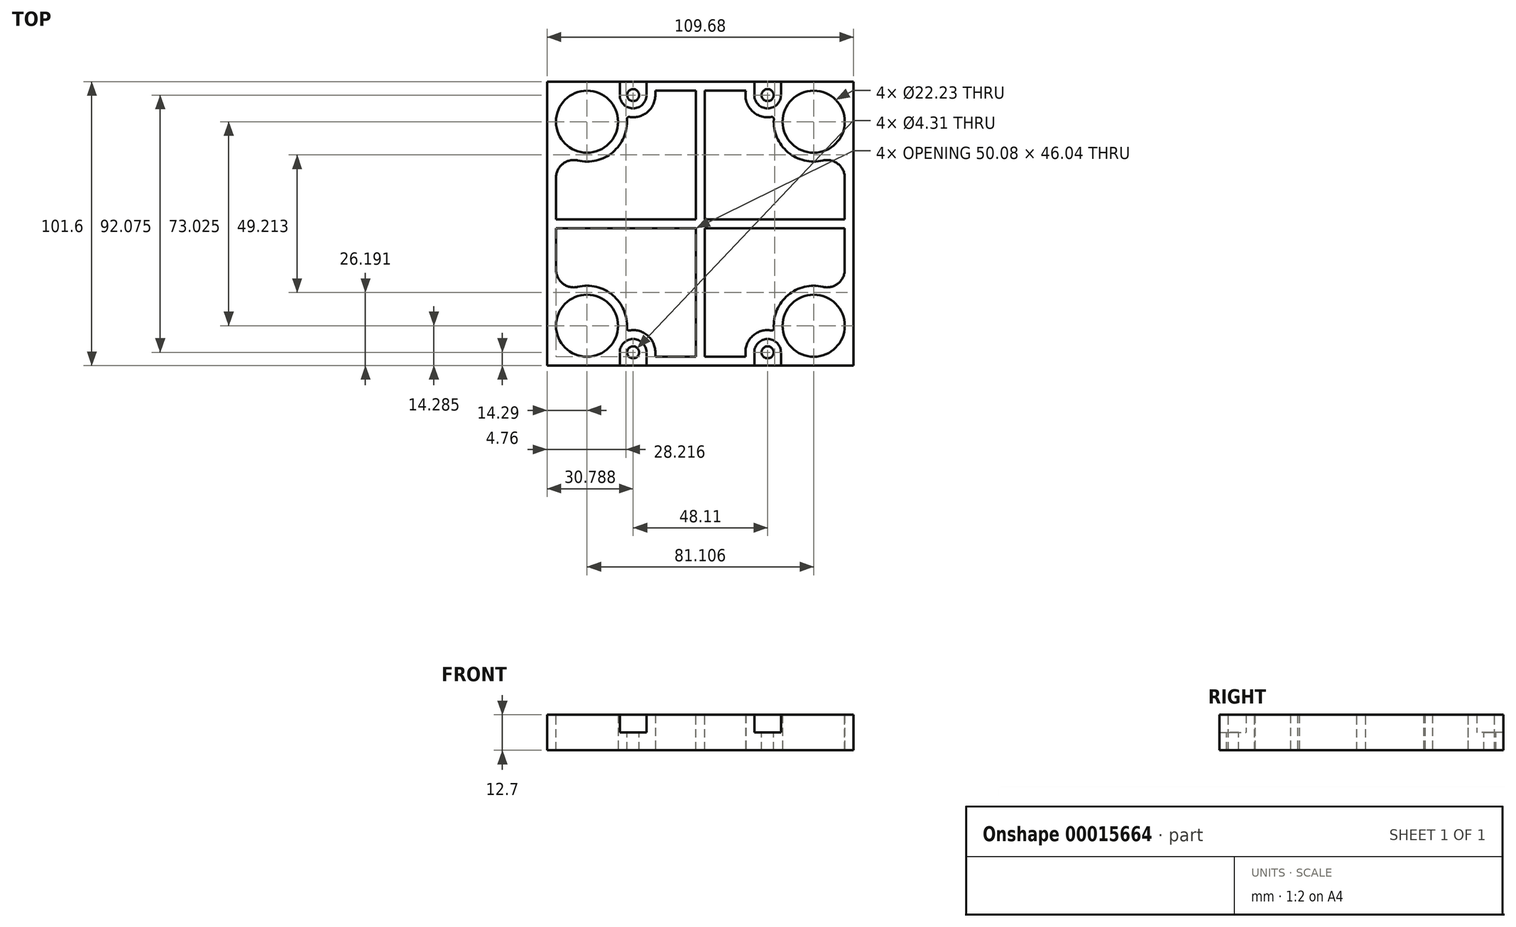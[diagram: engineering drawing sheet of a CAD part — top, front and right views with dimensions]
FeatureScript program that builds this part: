
annotation { "Feature Type Name" : "Feature", "Feature Type Description" : "" }
export const myFeature = defineFeature(function(context is Context, id is Id, definition is map)
    precondition{}
    {
        {
            var Q0;
            Q0=qCreatedBy(makeId("Top.planeOp"),FACE);
            var sketch = newSketch(context, id + "F0", { "sketchPlane" : qUnion([Q0])});
            skCircle(sketch, "E0", {"center": v(0, 0) * mm, "radius": 11.11 * mm});
            skLineSegment(sketch, "E1", {"start": v(0, 0) * mm, "end": v(81.1, 0) * mm, "construction": true});
            skLineSegment(sketch, "E2.left", {"start": v(-14.29, 14.29) * mm, "end": v(-14.29, -87.31) * mm});
            skLineSegment(sketch, "E2.right", {"start": v(95.4, 14.29) * mm, "end": v(95.4, -87.31) * mm});
            skPoint(sketch, "E2.middle", {"position": v(40.55, -36.51) * mm});
            skLineSegment(sketch, "E3", {"start": v(81.1, 0) * mm, "end": v(95.4, 0) * mm, "construction": true});
            skLineSegment(sketch, "E4", {"start": v(0, 0) * mm, "end": v(-14.29, 0) * mm, "construction": true});
            skCircle(sketch, "E5", {"center": v(81.1, 0) * mm, "radius": 11.11 * mm});
            skLineSegment(sketch, "E6", {"start": v(-14.29, 14.29) * mm, "end": v(11.74, 14.29) * mm});
            skLineSegment(sketch, "E7", {"start": v(95.4, 14.29) * mm, "end": v(69.37, 14.29) * mm});
            skLineSegment(sketch, "E8.bottom", {"start": v(11.74, 14.29) * mm, "end": v(21.26, 14.29) * mm, "construction": true});
            skLineSegment(sketch, "E8.top", {"start": v(11.74, 9.52) * mm, "end": v(21.26, 9.52) * mm, "construction": true});
            skLineSegment(sketch, "E8.left", {"start": v(11.74, 14.29) * mm, "end": v(11.74, 9.52) * mm});
            skLineSegment(sketch, "E8.right", {"start": v(21.26, 14.29) * mm, "end": v(21.26, 9.52) * mm});
            skLineSegment(sketch, "E9.bottom", {"start": v(69.37, 14.29) * mm, "end": v(59.85, 14.29) * mm, "construction": true});
            skLineSegment(sketch, "E9.top", {"start": v(69.37, 9.52) * mm, "end": v(59.85, 9.52) * mm, "construction": true});
            skLineSegment(sketch, "E9.left", {"start": v(69.37, 14.29) * mm, "end": v(69.37, 9.53) * mm});
            skLineSegment(sketch, "E9.right", {"start": v(59.85, 14.29) * mm, "end": v(59.85, 9.53) * mm});
            skCircle(sketch, "E10", {"center": v(16.5, 9.52) * mm, "radius": 7.94 * mm, "construction": true});
            skArc(sketch, "E11", {"start": v(21.26, 9.52) * mm, "mid": v(16.5, 14.29) * mm, "end": v(11.74, 9.52) * mm, "construction": true});
            skArc(sketch, "E12", {"start": v(11.74, 9.52) * mm, "mid": v(16.5, 4.76) * mm, "end": v(21.26, 9.52) * mm});
            skArc(sketch, "E13", {"start": v(59.85, 9.53) * mm, "mid": v(64.6, 4.76) * mm, "end": v(69.37, 9.53) * mm});
            skLineSegment(sketch, "E14", {"start": v(21.26, 14.29) * mm, "end": v(59.85, 14.29) * mm});
            skLineSegment(sketch, "E15", {"start": v(-14.29, -87.31) * mm, "end": v(11.74, -87.31) * mm});
            skLineSegment(sketch, "E16", {"start": v(95.4, -87.31) * mm, "end": v(69.37, -87.31) * mm});
            skLineSegment(sketch, "E17.bottom", {"start": v(11.74, -87.31) * mm, "end": v(21.26, -87.31) * mm, "construction": true});
            skLineSegment(sketch, "E17.top", {"start": v(11.74, -82.55) * mm, "end": v(21.26, -82.55) * mm, "construction": true});
            skLineSegment(sketch, "E17.left", {"start": v(11.74, -87.31) * mm, "end": v(11.74, -82.55) * mm});
            skLineSegment(sketch, "E17.right", {"start": v(21.26, -87.31) * mm, "end": v(21.26, -82.55) * mm});
            skLineSegment(sketch, "E18.bottom", {"start": v(69.37, -87.31) * mm, "end": v(59.85, -87.31) * mm, "construction": true});
            skLineSegment(sketch, "E18.top", {"start": v(69.37, -82.55) * mm, "end": v(59.85, -82.55) * mm, "construction": true});
            skLineSegment(sketch, "E18.left", {"start": v(69.37, -87.31) * mm, "end": v(69.37, -82.55) * mm});
            skLineSegment(sketch, "E18.right", {"start": v(59.85, -87.31) * mm, "end": v(59.85, -82.55) * mm});
            skLineSegment(sketch, "E19", {"start": v(21.26, -87.31) * mm, "end": v(59.85, -87.31) * mm});
            skArc(sketch, "E20", {"start": v(21.26, -82.55) * mm, "mid": v(16.5, -77.79) * mm, "end": v(11.74, -82.55) * mm});
            skArc(sketch, "E21", {"start": v(69.37, -82.55) * mm, "mid": v(64.6, -77.79) * mm, "end": v(59.85, -82.55) * mm});
            skLineSegment(sketch, "E22", {"start": v(40.55, 0) * mm, "end": v(40.55, 14.29) * mm, "construction": true});
            skLineSegment(sketch, "E23", {"start": v(-14.29, -73.03) * mm, "end": v(0, -73.03) * mm, "construction": true});
            skLineSegment(sketch, "E24", {"start": v(0, -73.03) * mm, "end": v(81.1, -73.03) * mm, "construction": true});
            skLineSegment(sketch, "E25", {"start": v(81.1, -73.03) * mm, "end": v(95.4, -73.03) * mm, "construction": true});
            skLineSegment(sketch, "E26", {"start": v(40.55, -73.03) * mm, "end": v(40.55, -87.31) * mm, "construction": true});
            skCircle(sketch, "E27", {"center": v(0, -73.02) * mm, "radius": 11.11 * mm});
            skCircle(sketch, "E28", {"center": v(81.1, -73.03) * mm, "radius": 11.11 * mm});
            skSolve(sketch);
        }
        {
            var Q0;
            Q0=qSketchRegion(id+"F0",true);
            extrude(context, id + "F1", {"entities" : qUnion([Q0]), "depth" : 6.35 * mm});
        }
        {
            var Q0;
            Q0=makeQuery(id+"F1.opExtrude","CAP_FACE",FACE,{"disambiguationData":[OSD([sQuery(id+"F0.wireOp",EDGE,"E0"),sQuery(id+"F0.wireOp",EDGE,"E2.left"),sQuery(id+"F0.wireOp",EDGE,"E2.right"),sQuery(id+"F0.wireOp",EDGE,"E5"),sQuery(id+"F0.wireOp",EDGE,"E6"),sQuery(id+"F0.wireOp",EDGE,"E7"),sQuery(id+"F0.wireOp",EDGE,"E8.left"),sQuery(id+"F0.wireOp",EDGE,"E8.right"),sQuery(id+"F0.wireOp",EDGE,"E9.left"),sQuery(id+"F0.wireOp",EDGE,"E9.right"),sQuery(id+"F0.wireOp",EDGE,"E12"),sQuery(id+"F0.wireOp",EDGE,"E13"),sQuery(id+"F0.wireOp",EDGE,"E14"),sQuery(id+"F0.wireOp",EDGE,"E15"),sQuery(id+"F0.wireOp",EDGE,"E16"),sQuery(id+"F0.wireOp",EDGE,"E17.left"),sQuery(id+"F0.wireOp",EDGE,"E17.right"),sQuery(id+"F0.wireOp",EDGE,"E18.left"),sQuery(id+"F0.wireOp",EDGE,"E18.right"),sQuery(id+"F0.wireOp",EDGE,"E19"),sQuery(id+"F0.wireOp",EDGE,"E20"),sQuery(id+"F0.wireOp",EDGE,"E21")])],"isStart":true});
            var sketch = newSketch(context, id + "F2", { "sketchPlane" : qUnion([Q0])});
            skLineSegment(sketch, "E29.bottom", {"start": v(11.74, -14.29) * mm, "end": v(69.37, -14.29) * mm});
            skLineSegment(sketch, "E29.top", {"start": v(11.74, 87.31) * mm, "end": v(69.37, 87.31) * mm});
            skLineSegment(sketch, "E29.left", {"start": v(11.74, -14.29) * mm, "end": v(11.74, 87.31) * mm, "construction": true});
            skLineSegment(sketch, "E29.right", {"start": v(69.37, -14.29) * mm, "end": v(69.37, 87.31) * mm, "construction": true});
            skCircle(sketch, "E30", {"center": v(16.5, 82.55) * mm, "radius": 2.15 * mm});
            skCircle(sketch, "E31", {"center": v(16.5, -9.52) * mm, "radius": 2.15 * mm});
            skCircle(sketch, "E32", {"center": v(64.6, 82.55) * mm, "radius": 2.15 * mm});
            skCircle(sketch, "E33", {"center": v(64.6, -9.53) * mm, "radius": 2.15 * mm});
            skSolve(sketch);
        }
        {
            var Q0;
            {var subQ19=sQuery(id+"F0.wireOp",EDGE,"E0");var subQ20=makeQuery(id+"F1.opExtrude","CAP_EDGE",EDGE,{"disambiguationData":[OSD([subQ19])],"isStart":true});Q0=makeQuery(id+"F2.imprint","IMPRINT",FACE,{"disambiguationData":[TD([[makeQuery(id+"F2.imprint","IMPRINT",EDGE,{"derivedFrom":subQ20}),1.0]])]});}
            var Q1;
            Q1=makeQuery(id+"F2.imprint","IMPRINT",FACE,{"disambiguationData":[TD([[makeQuery(id+"F2.imprint","IMPRINT",EDGE,{"derivedFrom":sQuery(id+"F2.wireOp",EDGE,"E31")}),-1.0]])]});
            var Q2;
            Q2=makeQuery(id+"F2.imprint","IMPRINT",FACE,{"disambiguationData":[TD([[makeQuery(id+"F2.imprint","IMPRINT",EDGE,{"derivedFrom":sQuery(id+"F2.wireOp",EDGE,"E33")}),-1.0]])]});
            var Q3;
            Q3=makeQuery(id+"F2.imprint","IMPRINT",FACE,{"disambiguationData":[TD([[makeQuery(id+"F2.imprint","IMPRINT",EDGE,{"derivedFrom":sQuery(id+"F2.wireOp",EDGE,"E32")}),-1.0]])]});
            var Q4;
            Q4=makeQuery(id+"F2.imprint","IMPRINT",FACE,{"disambiguationData":[TD([[makeQuery(id+"F2.imprint","IMPRINT",EDGE,{"derivedFrom":sQuery(id+"F2.wireOp",EDGE,"E30")}),-1.0]])]});
            extrude(context, id + "F3", {"entities" : qUnion([Q0, Q1, Q2, Q3, Q4]), "operationType" : NewBodyOperationType.ADD, "depth" : 6.35 * mm});
        }
        {
            var Q0;
            {var subQ0=sQuery(id+"F0.wireOp",EDGE,"E28");var subQ1=sQuery(id+"F0.wireOp",EDGE,"E27");var subQ2=sQuery(id+"F0.wireOp",EDGE,"E21");var subQ3=sQuery(id+"F0.wireOp",EDGE,"E20");var subQ4=sQuery(id+"F0.wireOp",EDGE,"E19");var subQ5=sQuery(id+"F0.wireOp",EDGE,"E18.right");var subQ6=sQuery(id+"F0.wireOp",EDGE,"E18.left");var subQ7=sQuery(id+"F0.wireOp",EDGE,"E17.right");var subQ8=sQuery(id+"F0.wireOp",EDGE,"E17.left");var subQ9=sQuery(id+"F0.wireOp",EDGE,"E16");var subQ10=sQuery(id+"F0.wireOp",EDGE,"E15");var subQ11=sQuery(id+"F0.wireOp",EDGE,"E14");var subQ12=sQuery(id+"F0.wireOp",EDGE,"E13");var subQ13=sQuery(id+"F0.wireOp",EDGE,"E12");var subQ14=sQuery(id+"F0.wireOp",EDGE,"E9.right");var subQ15=sQuery(id+"F0.wireOp",EDGE,"E9.left");var subQ16=sQuery(id+"F0.wireOp",EDGE,"E8.right");var subQ17=sQuery(id+"F0.wireOp",EDGE,"E8.left");var subQ18=sQuery(id+"F0.wireOp",EDGE,"E7");var subQ19=sQuery(id+"F0.wireOp",EDGE,"E6");var subQ20=sQuery(id+"F0.wireOp",EDGE,"E5");var subQ21=sQuery(id+"F0.wireOp",EDGE,"E2.right");var subQ22=sQuery(id+"F0.wireOp",EDGE,"E2.left");var subQ23=sQuery(id+"F0.wireOp",EDGE,"E0");Q0=makeQuery(id+"FTSSr8BHqQrdgFx_1.boolean.opBoolean","MERGE",FACE,{"derivedFrom":[makeQuery(id+"F1.opExtrude","CAP_FACE",FACE,{"disambiguationData":[OSD([subQ23,subQ22,subQ21,subQ20,subQ19,subQ18,subQ17,subQ16,subQ15,subQ14,subQ13,subQ12,subQ11,subQ10,subQ9,subQ8,subQ7,subQ6,subQ5,subQ4,subQ3,subQ2,subQ1,subQ0])],"isStart":false}),makeQuery(id+"FTSSr8BHqQrdgFx_1.opExtrude","CAP_FACE",FACE,{"disambiguationData":[OSD([subQ23,subQ22,subQ21,subQ20,subQ19,subQ18,subQ17,subQ16,subQ15,subQ14,subQ13,subQ12,subQ11,subQ10,subQ9,subQ8,subQ7,subQ6,subQ5,subQ4,subQ3,subQ2,subQ1,subQ0]),ownerDisambiguation([makeQuery(id+"FTSSr8BHqQrdgFx_1.opExtrude","SWEPT_BODY",BODY,{"disambiguationData":[OSD([subQ23,subQ22,subQ21,subQ20,subQ19,subQ18,subQ17,subQ16,subQ15,subQ14,subQ13,subQ12,subQ11,subQ10,subQ9,subQ8,subQ7,subQ6,subQ5,subQ4,subQ3,subQ2,subQ1,subQ0]),TDD([makeQuery(id+"Fb57pSd5HtlTtCQ_1.opShell","OFFSET_FACE",FACE,{"disambiguationData":[OSD([subQ23,subQ22,subQ21,subQ20,subQ19,subQ18,subQ17,subQ16,subQ15,subQ14,subQ13,subQ12,subQ11,subQ10,subQ9,subQ8,subQ7,subQ6,subQ5,subQ4,subQ3,subQ2,subQ1,subQ0]),OD(0.0)]})])]})])],"isStart":false}),makeQuery(id+"FTSSr8BHqQrdgFx_1.opExtrude","CAP_FACE",FACE,{"disambiguationData":[OSD([subQ23,subQ22,subQ21,subQ20,subQ19,subQ18,subQ17,subQ16,subQ15,subQ14,subQ13,subQ12,subQ11,subQ10,subQ9,subQ8,subQ7,subQ6,subQ5,subQ4,subQ3,subQ2,subQ1,subQ0]),ownerDisambiguation([makeQuery(id+"FTSSr8BHqQrdgFx_1.opExtrude","SWEPT_BODY",BODY,{"disambiguationData":[OSD([subQ23,subQ22,subQ21,subQ20,subQ19,subQ18,subQ17,subQ16,subQ15,subQ14,subQ13,subQ12,subQ11,subQ10,subQ9,subQ8,subQ7,subQ6,subQ5,subQ4,subQ3,subQ2,subQ1,subQ0]),TDD([makeQuery(id+"Fb57pSd5HtlTtCQ_1.opShell","OFFSET_FACE",FACE,{"disambiguationData":[OSD([subQ23,subQ22,subQ21,subQ20,subQ19,subQ18,subQ17,subQ16,subQ15,subQ14,subQ13,subQ12,subQ11,subQ10,subQ9,subQ8,subQ7,subQ6,subQ5,subQ4,subQ3,subQ2,subQ1,subQ0]),OD(1.0)]})])]})])],"isStart":false}),makeQuery(id+"FTSSr8BHqQrdgFx_1.opExtrude","CAP_FACE",FACE,{"disambiguationData":[OSD([subQ23,subQ22,subQ21,subQ20,subQ19,subQ18,subQ17,subQ16,subQ15,subQ14,subQ13,subQ12,subQ11,subQ10,subQ9,subQ8,subQ7,subQ6,subQ5,subQ4,subQ3,subQ2,subQ1,subQ0]),ownerDisambiguation([makeQuery(id+"FTSSr8BHqQrdgFx_1.opExtrude","SWEPT_BODY",BODY,{"disambiguationData":[OSD([subQ23,subQ22,subQ21,subQ20,subQ19,subQ18,subQ17,subQ16,subQ15,subQ14,subQ13,subQ12,subQ11,subQ10,subQ9,subQ8,subQ7,subQ6,subQ5,subQ4,subQ3,subQ2,subQ1,subQ0]),TDD([makeQuery(id+"Fb57pSd5HtlTtCQ_1.opShell","OFFSET_FACE",FACE,{"disambiguationData":[OSD([subQ23,subQ22,subQ21,subQ20,subQ19,subQ18,subQ17,subQ16,subQ15,subQ14,subQ13,subQ12,subQ11,subQ10,subQ9,subQ8,subQ7,subQ6,subQ5,subQ4,subQ3,subQ2,subQ1,subQ0]),OD(4.0)]})])]})])],"isStart":false}),makeQuery(id+"FTSSr8BHqQrdgFx_1.opExtrude","CAP_FACE",FACE,{"disambiguationData":[OSD([subQ23,subQ22,subQ21,subQ20,subQ19,subQ18,subQ17,subQ16,subQ15,subQ14,subQ13,subQ12,subQ11,subQ10,subQ9,subQ8,subQ7,subQ6,subQ5,subQ4,subQ3,subQ2,subQ1,subQ0]),ownerDisambiguation([makeQuery(id+"FTSSr8BHqQrdgFx_1.opExtrude","SWEPT_BODY",BODY,{"disambiguationData":[OSD([subQ23,subQ22,subQ21,subQ20,subQ19,subQ18,subQ17,subQ16,subQ15,subQ14,subQ13,subQ12,subQ11,subQ10,subQ9,subQ8,subQ7,subQ6,subQ5,subQ4,subQ3,subQ2,subQ1,subQ0]),TDD([makeQuery(id+"Fb57pSd5HtlTtCQ_1.opShell","OFFSET_FACE",FACE,{"disambiguationData":[OSD([subQ23,subQ22,subQ21,subQ20,subQ19,subQ18,subQ17,subQ16,subQ15,subQ14,subQ13,subQ12,subQ11,subQ10,subQ9,subQ8,subQ7,subQ6,subQ5,subQ4,subQ3,subQ2,subQ1,subQ0]),OD(3.0)]})])]})])],"isStart":false})]});}
            shell(context, id + "F4", {"entities" : qUnion([Q0]), "thickness" : 3.17 * mm});
        }
        {
            var Q0;
            Q0=makeQuery(id+"F4.opShell","OFFSET_FACE",FACE,{"disambiguationData":[OSD([sQuery(id+"F0.wireOp",EDGE,"E0"),sQuery(id+"F0.wireOp",EDGE,"E2.left"),sQuery(id+"F0.wireOp",EDGE,"E2.right"),sQuery(id+"F0.wireOp",EDGE,"E5"),sQuery(id+"F0.wireOp",EDGE,"E6"),sQuery(id+"F0.wireOp",EDGE,"E7"),sQuery(id+"F0.wireOp",EDGE,"E8.left"),sQuery(id+"F0.wireOp",EDGE,"E8.right"),sQuery(id+"F0.wireOp",EDGE,"E9.left"),sQuery(id+"F0.wireOp",EDGE,"E9.right"),sQuery(id+"F0.wireOp",EDGE,"E12"),sQuery(id+"F0.wireOp",EDGE,"E13"),sQuery(id+"F0.wireOp",EDGE,"E14"),sQuery(id+"F0.wireOp",EDGE,"E15"),sQuery(id+"F0.wireOp",EDGE,"E16"),sQuery(id+"F0.wireOp",EDGE,"E17.left"),sQuery(id+"F0.wireOp",EDGE,"E17.right"),sQuery(id+"F0.wireOp",EDGE,"E18.left"),sQuery(id+"F0.wireOp",EDGE,"E18.right"),sQuery(id+"F0.wireOp",EDGE,"E19"),sQuery(id+"F0.wireOp",EDGE,"E20"),sQuery(id+"F0.wireOp",EDGE,"E21"),sQuery(id+"F0.wireOp",EDGE,"E27"),sQuery(id+"F0.wireOp",EDGE,"E28"),sQuery(id+"F2.wireOp",EDGE,"E29.bottom"),sQuery(id+"F2.wireOp",EDGE,"E29.top"),sQuery(id+"F2.wireOp",EDGE,"E30"),sQuery(id+"F2.wireOp",EDGE,"E31"),sQuery(id+"F2.wireOp",EDGE,"E32"),sQuery(id+"F2.wireOp",EDGE,"E33")]),OD(0.0)]});
            var Q1;
            Q1=makeQuery(id+"F3.opExtrude","CAP_FACE",FACE,{"disambiguationData":[OSD([sQuery(id+"F0.wireOp",EDGE,"E0"),sQuery(id+"F0.wireOp",EDGE,"E2.left"),sQuery(id+"F0.wireOp",EDGE,"E2.right"),sQuery(id+"F0.wireOp",EDGE,"E5"),sQuery(id+"F0.wireOp",EDGE,"E6"),sQuery(id+"F0.wireOp",EDGE,"E7"),sQuery(id+"F0.wireOp",EDGE,"E8.left"),sQuery(id+"F0.wireOp",EDGE,"E8.right"),sQuery(id+"F0.wireOp",EDGE,"E9.left"),sQuery(id+"F0.wireOp",EDGE,"E9.right"),sQuery(id+"F0.wireOp",EDGE,"E12"),sQuery(id+"F0.wireOp",EDGE,"E13"),sQuery(id+"F0.wireOp",EDGE,"E14"),sQuery(id+"F0.wireOp",EDGE,"E15"),sQuery(id+"F0.wireOp",EDGE,"E16"),sQuery(id+"F0.wireOp",EDGE,"E17.left"),sQuery(id+"F0.wireOp",EDGE,"E17.right"),sQuery(id+"F0.wireOp",EDGE,"E18.left"),sQuery(id+"F0.wireOp",EDGE,"E18.right"),sQuery(id+"F0.wireOp",EDGE,"E19"),sQuery(id+"F0.wireOp",EDGE,"E20"),sQuery(id+"F0.wireOp",EDGE,"E21"),sQuery(id+"F0.wireOp",EDGE,"E27"),sQuery(id+"F0.wireOp",EDGE,"E28"),sQuery(id+"F2.wireOp",EDGE,"E29.bottom"),sQuery(id+"F2.wireOp",EDGE,"E29.top"),sQuery(id+"F2.wireOp",EDGE,"E30"),sQuery(id+"F2.wireOp",EDGE,"E31"),sQuery(id+"F2.wireOp",EDGE,"E32"),sQuery(id+"F2.wireOp",EDGE,"E33")])],"isStart":false});
            extrude(context, id + "F5", {"entities" : qUnion([Q0]), "operationType" : NewBodyOperationType.REMOVE, "endBound" : BoundingType.UP_TO_SURFACE, "oppositeDirection" : true, "endBoundEntityFace" : qUnion([Q1]), "depth" : 25.4 * mm});
        }
        {
            var Q0;
            Q0=makeQuery(id+"F4.opShell","OFFSET_FACE",FACE,{"disambiguationData":[OSD([sQuery(id+"F0.wireOp",EDGE,"E0"),sQuery(id+"F0.wireOp",EDGE,"E2.left"),sQuery(id+"F0.wireOp",EDGE,"E2.right"),sQuery(id+"F0.wireOp",EDGE,"E5"),sQuery(id+"F0.wireOp",EDGE,"E6"),sQuery(id+"F0.wireOp",EDGE,"E7"),sQuery(id+"F0.wireOp",EDGE,"E8.left"),sQuery(id+"F0.wireOp",EDGE,"E8.right"),sQuery(id+"F0.wireOp",EDGE,"E9.left"),sQuery(id+"F0.wireOp",EDGE,"E9.right"),sQuery(id+"F0.wireOp",EDGE,"E12"),sQuery(id+"F0.wireOp",EDGE,"E13"),sQuery(id+"F0.wireOp",EDGE,"E14"),sQuery(id+"F0.wireOp",EDGE,"E15"),sQuery(id+"F0.wireOp",EDGE,"E16"),sQuery(id+"F0.wireOp",EDGE,"E17.left"),sQuery(id+"F0.wireOp",EDGE,"E17.right"),sQuery(id+"F0.wireOp",EDGE,"E18.left"),sQuery(id+"F0.wireOp",EDGE,"E18.right"),sQuery(id+"F0.wireOp",EDGE,"E19"),sQuery(id+"F0.wireOp",EDGE,"E20"),sQuery(id+"F0.wireOp",EDGE,"E21"),sQuery(id+"F0.wireOp",EDGE,"E27"),sQuery(id+"F0.wireOp",EDGE,"E28"),sQuery(id+"F2.wireOp",EDGE,"E29.bottom"),sQuery(id+"F2.wireOp",EDGE,"E29.top"),sQuery(id+"F2.wireOp",EDGE,"E30"),sQuery(id+"F2.wireOp",EDGE,"E31"),sQuery(id+"F2.wireOp",EDGE,"E32"),sQuery(id+"F2.wireOp",EDGE,"E33")]),OD(1.0)]});
            var Q1;
            Q1=makeQuery(id+"F4.opShell","OFFSET_FACE",FACE,{"disambiguationData":[OSD([sQuery(id+"F0.wireOp",EDGE,"E0"),sQuery(id+"F0.wireOp",EDGE,"E2.left"),sQuery(id+"F0.wireOp",EDGE,"E2.right"),sQuery(id+"F0.wireOp",EDGE,"E5"),sQuery(id+"F0.wireOp",EDGE,"E6"),sQuery(id+"F0.wireOp",EDGE,"E7"),sQuery(id+"F0.wireOp",EDGE,"E15"),sQuery(id+"F0.wireOp",EDGE,"E16"),sQuery(id+"F0.wireOp",EDGE,"E27"),sQuery(id+"F0.wireOp",EDGE,"E28"),sQuery(id+"F2.wireOp",EDGE,"E29.bottom"),sQuery(id+"F2.wireOp",EDGE,"E29.top"),sQuery(id+"F2.wireOp",EDGE,"E30"),sQuery(id+"F2.wireOp",EDGE,"E31"),sQuery(id+"F2.wireOp",EDGE,"E32"),sQuery(id+"F2.wireOp",EDGE,"E33")]),OD(3.0)]});
            var Q2;
            Q2=makeQuery(id+"F4.opShell","OFFSET_FACE",FACE,{"disambiguationData":[OSD([sQuery(id+"F0.wireOp",EDGE,"E0"),sQuery(id+"F0.wireOp",EDGE,"E2.left"),sQuery(id+"F0.wireOp",EDGE,"E2.right"),sQuery(id+"F0.wireOp",EDGE,"E5"),sQuery(id+"F0.wireOp",EDGE,"E6"),sQuery(id+"F0.wireOp",EDGE,"E7"),sQuery(id+"F0.wireOp",EDGE,"E15"),sQuery(id+"F0.wireOp",EDGE,"E16"),sQuery(id+"F0.wireOp",EDGE,"E27"),sQuery(id+"F0.wireOp",EDGE,"E28"),sQuery(id+"F2.wireOp",EDGE,"E29.bottom"),sQuery(id+"F2.wireOp",EDGE,"E29.top"),sQuery(id+"F2.wireOp",EDGE,"E30"),sQuery(id+"F2.wireOp",EDGE,"E31"),sQuery(id+"F2.wireOp",EDGE,"E32"),sQuery(id+"F2.wireOp",EDGE,"E33")]),OD(4.0)]});
            var Q3;
            Q3=makeQuery(id+"F4.opShell","OFFSET_FACE",FACE,{"disambiguationData":[OSD([sQuery(id+"F0.wireOp",EDGE,"E0"),sQuery(id+"F0.wireOp",EDGE,"E2.left"),sQuery(id+"F0.wireOp",EDGE,"E2.right"),sQuery(id+"F0.wireOp",EDGE,"E5"),sQuery(id+"F0.wireOp",EDGE,"E6"),sQuery(id+"F0.wireOp",EDGE,"E7"),sQuery(id+"F0.wireOp",EDGE,"E15"),sQuery(id+"F0.wireOp",EDGE,"E16"),sQuery(id+"F0.wireOp",EDGE,"E27"),sQuery(id+"F0.wireOp",EDGE,"E28"),sQuery(id+"F2.wireOp",EDGE,"E29.bottom"),sQuery(id+"F2.wireOp",EDGE,"E29.top"),sQuery(id+"F2.wireOp",EDGE,"E30"),sQuery(id+"F2.wireOp",EDGE,"E31"),sQuery(id+"F2.wireOp",EDGE,"E32"),sQuery(id+"F2.wireOp",EDGE,"E33")]),OD(2.0)]});
            var Q4;
            Q4=makeQuery(id+"F1.opExtrude","CAP_FACE",FACE,{"disambiguationData":[OSD([sQuery(id+"F0.wireOp",EDGE,"E0"),sQuery(id+"F0.wireOp",EDGE,"E2.left"),sQuery(id+"F0.wireOp",EDGE,"E2.right"),sQuery(id+"F0.wireOp",EDGE,"E5"),sQuery(id+"F0.wireOp",EDGE,"E6"),sQuery(id+"F0.wireOp",EDGE,"E7"),sQuery(id+"F0.wireOp",EDGE,"E8.left"),sQuery(id+"F0.wireOp",EDGE,"E8.right"),sQuery(id+"F0.wireOp",EDGE,"E9.left"),sQuery(id+"F0.wireOp",EDGE,"E9.right"),sQuery(id+"F0.wireOp",EDGE,"E12"),sQuery(id+"F0.wireOp",EDGE,"E13"),sQuery(id+"F0.wireOp",EDGE,"E14"),sQuery(id+"F0.wireOp",EDGE,"E15"),sQuery(id+"F0.wireOp",EDGE,"E16"),sQuery(id+"F0.wireOp",EDGE,"E17.left"),sQuery(id+"F0.wireOp",EDGE,"E17.right"),sQuery(id+"F0.wireOp",EDGE,"E18.left"),sQuery(id+"F0.wireOp",EDGE,"E18.right"),sQuery(id+"F0.wireOp",EDGE,"E19"),sQuery(id+"F0.wireOp",EDGE,"E20"),sQuery(id+"F0.wireOp",EDGE,"E21"),sQuery(id+"F0.wireOp",EDGE,"E27"),sQuery(id+"F0.wireOp",EDGE,"E28")])],"isStart":false});
            extrude(context, id + "F6", {"entities" : qUnion([Q0, Q1, Q2, Q3]), "operationType" : NewBodyOperationType.ADD, "endBound" : BoundingType.UP_TO_SURFACE, "endBoundEntityFace" : qUnion([Q4]), "depth" : 25.4 * mm});
        }
        {
            var Q0;
            {var subQ0=sQuery(id+"F0.wireOp",EDGE,"E27");var subQ1=makeQuery(id+"F3.boolean.opBoolean","MERGE",FACE,{"derivedFrom":[makeQuery(id+"F1.opExtrude","SWEPT_FACE",FACE,{"disambiguationData":[OSD([subQ0])]}),makeQuery(id+"F3.opExtrude","SWEPT_FACE",FACE,{"disambiguationData":[OSD([subQ0])]})]});var subQ2=sQuery(id+"F0.wireOp",EDGE,"E2.left");var subQ3=makeQuery(id+"F3.boolean.opBoolean","MERGE",FACE,{"derivedFrom":[makeQuery(id+"F1.opExtrude","SWEPT_FACE",FACE,{"disambiguationData":[OSD([subQ2])]}),makeQuery(id+"F3.opExtrude","SWEPT_FACE",FACE,{"disambiguationData":[OSD([subQ2])]})]});var subQ4=sQuery(id+"F2.wireOp",EDGE,"E33");var subQ5=sQuery(id+"F2.wireOp",EDGE,"E32");var subQ6=sQuery(id+"F2.wireOp",EDGE,"E31");var subQ7=sQuery(id+"F2.wireOp",EDGE,"E30");var subQ8=sQuery(id+"F2.wireOp",EDGE,"E29.top");var subQ9=sQuery(id+"F2.wireOp",EDGE,"E29.bottom");var subQ10=sQuery(id+"F0.wireOp",EDGE,"E28");var subQ11=sQuery(id+"F0.wireOp",EDGE,"E16");var subQ12=sQuery(id+"F0.wireOp",EDGE,"E15");var subQ13=sQuery(id+"F0.wireOp",EDGE,"E7");var subQ14=sQuery(id+"F0.wireOp",EDGE,"E6");var subQ15=sQuery(id+"F0.wireOp",EDGE,"E5");var subQ16=sQuery(id+"F0.wireOp",EDGE,"E2.right");var subQ17=sQuery(id+"F0.wireOp",EDGE,"E0");Q0=makeQuery(id+"F5.boolean.opBoolean","MERGE",EDGE,{"derivedFrom":[makeQuery(id+"F4.opShell","TWEAK_EDGE",EDGE,{"disambiguationData":[OD(1.0)],"derivedFrom":[subQ3,subQ1]}),makeQuery(id+"F5.opExtrude","SWEPT_EDGE",EDGE,{"disambiguationData":[OSD([subQ17,subQ2,subQ16,subQ15,subQ14,subQ13,subQ12,subQ11,subQ0,subQ10,subQ9,subQ8,subQ7,subQ6,subQ5,subQ4]),TDD([makeQuery(id+"F4.opShell","TWEAK_VERTEX",VERTEX,{"disambiguationData":[OD(0.0)],"derivedFrom":[makeQuery(id+"F3.opExtrude","CAP_FACE",FACE,{"disambiguationData":[OSD([subQ17,subQ2,subQ16,subQ15,subQ14,subQ13,subQ12,subQ11,subQ0,subQ10,subQ9,subQ8,subQ7,subQ6,subQ5,subQ4])],"isStart":false}),subQ3,subQ1]})])]})]});}
            var Q1;
            {var subQ0=sQuery(id+"F0.wireOp",EDGE,"E2.left");var subQ1=makeQuery(id+"F3.boolean.opBoolean","MERGE",FACE,{"derivedFrom":[makeQuery(id+"F1.opExtrude","SWEPT_FACE",FACE,{"disambiguationData":[OSD([subQ0])]}),makeQuery(id+"F3.opExtrude","SWEPT_FACE",FACE,{"disambiguationData":[OSD([subQ0])]})]});var subQ2=sQuery(id+"F0.wireOp",EDGE,"E0");var subQ3=makeQuery(id+"F3.boolean.opBoolean","MERGE",FACE,{"derivedFrom":[makeQuery(id+"F1.opExtrude","SWEPT_FACE",FACE,{"disambiguationData":[OSD([subQ2])]}),makeQuery(id+"F3.opExtrude","SWEPT_FACE",FACE,{"disambiguationData":[OSD([subQ2])]})]});var subQ4=sQuery(id+"F2.wireOp",EDGE,"E33");var subQ5=sQuery(id+"F2.wireOp",EDGE,"E32");var subQ6=sQuery(id+"F2.wireOp",EDGE,"E31");var subQ7=sQuery(id+"F2.wireOp",EDGE,"E30");var subQ8=sQuery(id+"F2.wireOp",EDGE,"E29.top");var subQ9=sQuery(id+"F2.wireOp",EDGE,"E29.bottom");var subQ10=sQuery(id+"F0.wireOp",EDGE,"E28");var subQ11=sQuery(id+"F0.wireOp",EDGE,"E27");var subQ12=sQuery(id+"F0.wireOp",EDGE,"E16");var subQ13=sQuery(id+"F0.wireOp",EDGE,"E15");var subQ14=sQuery(id+"F0.wireOp",EDGE,"E7");var subQ15=sQuery(id+"F0.wireOp",EDGE,"E6");var subQ16=sQuery(id+"F0.wireOp",EDGE,"E5");var subQ17=sQuery(id+"F0.wireOp",EDGE,"E2.right");Q1=makeQuery(id+"F5.boolean.opBoolean","MERGE",EDGE,{"derivedFrom":[makeQuery(id+"F4.opShell","TWEAK_EDGE",EDGE,{"disambiguationData":[OD(0.0)],"derivedFrom":[subQ3,subQ1]}),makeQuery(id+"F5.opExtrude","SWEPT_EDGE",EDGE,{"disambiguationData":[OSD([subQ2,subQ0,subQ17,subQ16,subQ15,subQ14,subQ13,subQ12,subQ11,subQ10,subQ9,subQ8,subQ7,subQ6,subQ5,subQ4]),TDD([makeQuery(id+"F4.opShell","TWEAK_VERTEX",VERTEX,{"disambiguationData":[OD(0.0)],"derivedFrom":[makeQuery(id+"F3.opExtrude","CAP_FACE",FACE,{"disambiguationData":[OSD([subQ2,subQ0,subQ17,subQ16,subQ15,subQ14,subQ13,subQ12,subQ11,subQ10,subQ9,subQ8,subQ7,subQ6,subQ5,subQ4])],"isStart":false}),subQ3,subQ1]})])]})]});}
            var Q2;
            {var subQ0=sQuery(id+"F0.wireOp",EDGE,"E5");var subQ1=makeQuery(id+"F3.boolean.opBoolean","MERGE",FACE,{"derivedFrom":[makeQuery(id+"F1.opExtrude","SWEPT_FACE",FACE,{"disambiguationData":[OSD([subQ0])]}),makeQuery(id+"F3.opExtrude","SWEPT_FACE",FACE,{"disambiguationData":[OSD([subQ0])]})]});var subQ2=sQuery(id+"F0.wireOp",EDGE,"E2.right");var subQ3=makeQuery(id+"F3.boolean.opBoolean","MERGE",FACE,{"derivedFrom":[makeQuery(id+"F1.opExtrude","SWEPT_FACE",FACE,{"disambiguationData":[OSD([subQ2])]}),makeQuery(id+"F3.opExtrude","SWEPT_FACE",FACE,{"disambiguationData":[OSD([subQ2])]})]});var subQ4=sQuery(id+"F2.wireOp",EDGE,"E33");var subQ5=sQuery(id+"F2.wireOp",EDGE,"E32");var subQ6=sQuery(id+"F2.wireOp",EDGE,"E31");var subQ7=sQuery(id+"F2.wireOp",EDGE,"E30");var subQ8=sQuery(id+"F2.wireOp",EDGE,"E29.top");var subQ9=sQuery(id+"F2.wireOp",EDGE,"E29.bottom");var subQ10=sQuery(id+"F0.wireOp",EDGE,"E28");var subQ11=sQuery(id+"F0.wireOp",EDGE,"E27");var subQ12=sQuery(id+"F0.wireOp",EDGE,"E16");var subQ13=sQuery(id+"F0.wireOp",EDGE,"E15");var subQ14=sQuery(id+"F0.wireOp",EDGE,"E7");var subQ15=sQuery(id+"F0.wireOp",EDGE,"E6");var subQ16=sQuery(id+"F0.wireOp",EDGE,"E2.left");var subQ17=sQuery(id+"F0.wireOp",EDGE,"E0");Q2=makeQuery(id+"F5.boolean.opBoolean","MERGE",EDGE,{"derivedFrom":[makeQuery(id+"F4.opShell","TWEAK_EDGE",EDGE,{"disambiguationData":[OD(1.0)],"derivedFrom":[subQ3,subQ1]}),makeQuery(id+"F5.opExtrude","SWEPT_EDGE",EDGE,{"disambiguationData":[OSD([subQ17,subQ16,subQ2,subQ0,subQ15,subQ14,subQ13,subQ12,subQ11,subQ10,subQ9,subQ8,subQ7,subQ6,subQ5,subQ4]),TDD([makeQuery(id+"F4.opShell","TWEAK_VERTEX",VERTEX,{"disambiguationData":[OD(0.0)],"derivedFrom":[makeQuery(id+"F3.opExtrude","CAP_FACE",FACE,{"disambiguationData":[OSD([subQ17,subQ16,subQ2,subQ0,subQ15,subQ14,subQ13,subQ12,subQ11,subQ10,subQ9,subQ8,subQ7,subQ6,subQ5,subQ4])],"isStart":false}),subQ3,subQ1]})])]})]});}
            var Q3;
            {var subQ0=sQuery(id+"F0.wireOp",EDGE,"E28");var subQ1=makeQuery(id+"F3.boolean.opBoolean","MERGE",FACE,{"derivedFrom":[makeQuery(id+"F1.opExtrude","SWEPT_FACE",FACE,{"disambiguationData":[OSD([subQ0])]}),makeQuery(id+"F3.opExtrude","SWEPT_FACE",FACE,{"disambiguationData":[OSD([subQ0])]})]});var subQ2=sQuery(id+"F0.wireOp",EDGE,"E2.right");var subQ3=makeQuery(id+"F3.boolean.opBoolean","MERGE",FACE,{"derivedFrom":[makeQuery(id+"F1.opExtrude","SWEPT_FACE",FACE,{"disambiguationData":[OSD([subQ2])]}),makeQuery(id+"F3.opExtrude","SWEPT_FACE",FACE,{"disambiguationData":[OSD([subQ2])]})]});var subQ4=sQuery(id+"F2.wireOp",EDGE,"E33");var subQ5=sQuery(id+"F2.wireOp",EDGE,"E32");var subQ6=sQuery(id+"F2.wireOp",EDGE,"E31");var subQ7=sQuery(id+"F2.wireOp",EDGE,"E30");var subQ8=sQuery(id+"F2.wireOp",EDGE,"E29.top");var subQ9=sQuery(id+"F2.wireOp",EDGE,"E29.bottom");var subQ10=sQuery(id+"F0.wireOp",EDGE,"E27");var subQ11=sQuery(id+"F0.wireOp",EDGE,"E16");var subQ12=sQuery(id+"F0.wireOp",EDGE,"E15");var subQ13=sQuery(id+"F0.wireOp",EDGE,"E7");var subQ14=sQuery(id+"F0.wireOp",EDGE,"E6");var subQ15=sQuery(id+"F0.wireOp",EDGE,"E5");var subQ16=sQuery(id+"F0.wireOp",EDGE,"E2.left");var subQ17=sQuery(id+"F0.wireOp",EDGE,"E0");Q3=makeQuery(id+"F5.boolean.opBoolean","MERGE",EDGE,{"derivedFrom":[makeQuery(id+"F4.opShell","TWEAK_EDGE",EDGE,{"disambiguationData":[OD(1.0)],"derivedFrom":[subQ3,subQ1]}),makeQuery(id+"F5.opExtrude","SWEPT_EDGE",EDGE,{"disambiguationData":[OSD([subQ17,subQ16,subQ2,subQ15,subQ14,subQ13,subQ12,subQ11,subQ10,subQ0,subQ9,subQ8,subQ7,subQ6,subQ5,subQ4]),TDD([makeQuery(id+"F4.opShell","TWEAK_VERTEX",VERTEX,{"disambiguationData":[OD(0.0)],"derivedFrom":[makeQuery(id+"F3.opExtrude","CAP_FACE",FACE,{"disambiguationData":[OSD([subQ17,subQ16,subQ2,subQ15,subQ14,subQ13,subQ12,subQ11,subQ10,subQ0,subQ9,subQ8,subQ7,subQ6,subQ5,subQ4])],"isStart":false}),subQ3,subQ1]})])]})]});}
            fillet(context, id + "F7", {"entities" : qUnion([Q0, Q1, Q2, Q3]), "radius" : 6.35 * mm, "tangentPropagation" : true, "allowEdgeOverflow" : false});
        }
        {
            var Q0;
            {var subQ0=sQuery(id+"F0.wireOp",EDGE,"E27");var subQ1=sQuery(id+"F0.wireOp",EDGE,"E20");Q0=makeQuery(id+"F5.boolean.opBoolean","MERGE",EDGE,{"derivedFrom":[makeQuery(id+"F4.opShell","TWEAK_EDGE",EDGE,{"derivedFrom":[makeQuery(id+"F1.opExtrude","SWEPT_FACE",FACE,{"disambiguationData":[OSD([subQ1])]}),makeQuery(id+"F3.boolean.opBoolean","MERGE",FACE,{"derivedFrom":[makeQuery(id+"F1.opExtrude","SWEPT_FACE",FACE,{"disambiguationData":[OSD([subQ0])]}),makeQuery(id+"F3.opExtrude","SWEPT_FACE",FACE,{"disambiguationData":[OSD([subQ0])]})]})]}),makeQuery(id+"F5.opExtrude","SWEPT_EDGE",EDGE,{"disambiguationData":[OSD([sQuery(id+"F0.wireOp",EDGE,"E0"),sQuery(id+"F0.wireOp",EDGE,"E2.left"),sQuery(id+"F0.wireOp",EDGE,"E2.right"),sQuery(id+"F0.wireOp",EDGE,"E5"),sQuery(id+"F0.wireOp",EDGE,"E6"),sQuery(id+"F0.wireOp",EDGE,"E7"),sQuery(id+"F0.wireOp",EDGE,"E15"),sQuery(id+"F0.wireOp",EDGE,"E16"),subQ1,subQ0,sQuery(id+"F0.wireOp",EDGE,"E28"),sQuery(id+"F2.wireOp",EDGE,"E29.bottom"),sQuery(id+"F2.wireOp",EDGE,"E29.top"),sQuery(id+"F2.wireOp",EDGE,"E30"),sQuery(id+"F2.wireOp",EDGE,"E31"),sQuery(id+"F2.wireOp",EDGE,"E32"),sQuery(id+"F2.wireOp",EDGE,"E33")])]})]});}
            var Q1;
            {var subQ0=sQuery(id+"F0.wireOp",EDGE,"E12");var subQ1=sQuery(id+"F0.wireOp",EDGE,"E0");Q1=makeQuery(id+"F5.boolean.opBoolean","MERGE",EDGE,{"derivedFrom":[makeQuery(id+"F4.opShell","TWEAK_EDGE",EDGE,{"derivedFrom":[makeQuery(id+"F1.opExtrude","SWEPT_FACE",FACE,{"disambiguationData":[OSD([subQ0])]}),makeQuery(id+"F3.boolean.opBoolean","MERGE",FACE,{"derivedFrom":[makeQuery(id+"F1.opExtrude","SWEPT_FACE",FACE,{"disambiguationData":[OSD([subQ1])]}),makeQuery(id+"F3.opExtrude","SWEPT_FACE",FACE,{"disambiguationData":[OSD([subQ1])]})]})]}),makeQuery(id+"F5.opExtrude","SWEPT_EDGE",EDGE,{"disambiguationData":[OSD([subQ1,sQuery(id+"F0.wireOp",EDGE,"E2.left"),sQuery(id+"F0.wireOp",EDGE,"E2.right"),sQuery(id+"F0.wireOp",EDGE,"E5"),sQuery(id+"F0.wireOp",EDGE,"E6"),sQuery(id+"F0.wireOp",EDGE,"E7"),subQ0,sQuery(id+"F0.wireOp",EDGE,"E15"),sQuery(id+"F0.wireOp",EDGE,"E16"),sQuery(id+"F0.wireOp",EDGE,"E27"),sQuery(id+"F0.wireOp",EDGE,"E28"),sQuery(id+"F2.wireOp",EDGE,"E29.bottom"),sQuery(id+"F2.wireOp",EDGE,"E29.top"),sQuery(id+"F2.wireOp",EDGE,"E30"),sQuery(id+"F2.wireOp",EDGE,"E31"),sQuery(id+"F2.wireOp",EDGE,"E32"),sQuery(id+"F2.wireOp",EDGE,"E33")])]})]});}
            var Q2;
            {var subQ0=sQuery(id+"F0.wireOp",EDGE,"E13");var subQ1=sQuery(id+"F0.wireOp",EDGE,"E5");Q2=makeQuery(id+"F5.boolean.opBoolean","MERGE",EDGE,{"derivedFrom":[makeQuery(id+"F4.opShell","TWEAK_EDGE",EDGE,{"derivedFrom":[makeQuery(id+"F1.opExtrude","SWEPT_FACE",FACE,{"disambiguationData":[OSD([subQ0])]}),makeQuery(id+"F3.boolean.opBoolean","MERGE",FACE,{"derivedFrom":[makeQuery(id+"F1.opExtrude","SWEPT_FACE",FACE,{"disambiguationData":[OSD([subQ1])]}),makeQuery(id+"F3.opExtrude","SWEPT_FACE",FACE,{"disambiguationData":[OSD([subQ1])]})]})]}),makeQuery(id+"F5.opExtrude","SWEPT_EDGE",EDGE,{"disambiguationData":[OSD([sQuery(id+"F0.wireOp",EDGE,"E0"),sQuery(id+"F0.wireOp",EDGE,"E2.left"),sQuery(id+"F0.wireOp",EDGE,"E2.right"),subQ1,sQuery(id+"F0.wireOp",EDGE,"E6"),sQuery(id+"F0.wireOp",EDGE,"E7"),subQ0,sQuery(id+"F0.wireOp",EDGE,"E15"),sQuery(id+"F0.wireOp",EDGE,"E16"),sQuery(id+"F0.wireOp",EDGE,"E27"),sQuery(id+"F0.wireOp",EDGE,"E28"),sQuery(id+"F2.wireOp",EDGE,"E29.bottom"),sQuery(id+"F2.wireOp",EDGE,"E29.top"),sQuery(id+"F2.wireOp",EDGE,"E30"),sQuery(id+"F2.wireOp",EDGE,"E31"),sQuery(id+"F2.wireOp",EDGE,"E32"),sQuery(id+"F2.wireOp",EDGE,"E33")])]})]});}
            var Q3;
            {var subQ0=sQuery(id+"F0.wireOp",EDGE,"E28");var subQ1=sQuery(id+"F0.wireOp",EDGE,"E21");Q3=makeQuery(id+"F5.boolean.opBoolean","MERGE",EDGE,{"derivedFrom":[makeQuery(id+"F4.opShell","TWEAK_EDGE",EDGE,{"derivedFrom":[makeQuery(id+"F1.opExtrude","SWEPT_FACE",FACE,{"disambiguationData":[OSD([subQ1])]}),makeQuery(id+"F3.boolean.opBoolean","MERGE",FACE,{"derivedFrom":[makeQuery(id+"F1.opExtrude","SWEPT_FACE",FACE,{"disambiguationData":[OSD([subQ0])]}),makeQuery(id+"F3.opExtrude","SWEPT_FACE",FACE,{"disambiguationData":[OSD([subQ0])]})]})]}),makeQuery(id+"F5.opExtrude","SWEPT_EDGE",EDGE,{"disambiguationData":[OSD([sQuery(id+"F0.wireOp",EDGE,"E0"),sQuery(id+"F0.wireOp",EDGE,"E2.left"),sQuery(id+"F0.wireOp",EDGE,"E2.right"),sQuery(id+"F0.wireOp",EDGE,"E5"),sQuery(id+"F0.wireOp",EDGE,"E6"),sQuery(id+"F0.wireOp",EDGE,"E7"),sQuery(id+"F0.wireOp",EDGE,"E15"),sQuery(id+"F0.wireOp",EDGE,"E16"),subQ1,sQuery(id+"F0.wireOp",EDGE,"E27"),subQ0,sQuery(id+"F2.wireOp",EDGE,"E29.bottom"),sQuery(id+"F2.wireOp",EDGE,"E29.top"),sQuery(id+"F2.wireOp",EDGE,"E30"),sQuery(id+"F2.wireOp",EDGE,"E31"),sQuery(id+"F2.wireOp",EDGE,"E32"),sQuery(id+"F2.wireOp",EDGE,"E33")])]})]});}
            fillet(context, id + "F8", {"entities" : qUnion([Q0, Q1, Q2, Q3]), "radius" : 0.76 * mm, "tangentPropagation" : true, "allowEdgeOverflow" : false});
        }
        {
            var Q0;
            {var subQ0=sQuery(id+"F2.wireOp",EDGE,"E33");var subQ1=sQuery(id+"F2.wireOp",EDGE,"E32");var subQ2=sQuery(id+"F2.wireOp",EDGE,"E31");var subQ3=sQuery(id+"F2.wireOp",EDGE,"E30");var subQ4=sQuery(id+"F2.wireOp",EDGE,"E29.top");var subQ5=sQuery(id+"F2.wireOp",EDGE,"E29.bottom");var subQ6=sQuery(id+"F0.wireOp",EDGE,"E28");var subQ7=sQuery(id+"F0.wireOp",EDGE,"E27");var subQ8=sQuery(id+"F0.wireOp",EDGE,"E16");var subQ9=sQuery(id+"F0.wireOp",EDGE,"E15");var subQ10=sQuery(id+"F0.wireOp",EDGE,"E7");var subQ11=sQuery(id+"F0.wireOp",EDGE,"E6");var subQ12=sQuery(id+"F0.wireOp",EDGE,"E5");var subQ13=sQuery(id+"F0.wireOp",EDGE,"E2.right");var subQ14=sQuery(id+"F0.wireOp",EDGE,"E2.left");var subQ15=sQuery(id+"F0.wireOp",EDGE,"E0");var subQ16=sQuery(id+"F0.wireOp",EDGE,"E21");var subQ17=sQuery(id+"F0.wireOp",EDGE,"E20");var subQ18=sQuery(id+"F0.wireOp",EDGE,"E19");var subQ19=sQuery(id+"F0.wireOp",EDGE,"E18.right");var subQ20=sQuery(id+"F0.wireOp",EDGE,"E18.left");var subQ21=sQuery(id+"F0.wireOp",EDGE,"E17.right");var subQ22=sQuery(id+"F0.wireOp",EDGE,"E17.left");var subQ23=sQuery(id+"F0.wireOp",EDGE,"E14");var subQ24=sQuery(id+"F0.wireOp",EDGE,"E13");var subQ25=sQuery(id+"F0.wireOp",EDGE,"E12");var subQ26=sQuery(id+"F0.wireOp",EDGE,"E9.right");var subQ27=sQuery(id+"F0.wireOp",EDGE,"E9.left");var subQ28=sQuery(id+"F0.wireOp",EDGE,"E8.right");var subQ29=sQuery(id+"F0.wireOp",EDGE,"E8.left");Q0=makeQuery(id+"F6.boolean.opBoolean","MERGE",FACE,{"derivedFrom":[makeQuery(id+"F1.opExtrude","CAP_FACE",FACE,{"disambiguationData":[OSD([subQ15,subQ14,subQ13,subQ12,subQ11,subQ10,subQ29,subQ28,subQ27,subQ26,subQ25,subQ24,subQ23,subQ9,subQ8,subQ22,subQ21,subQ20,subQ19,subQ18,subQ17,subQ16,subQ7,subQ6])],"isStart":false}),makeQuery(id+"F6.opExtrude","CAP_FACE",FACE,{"disambiguationData":[OSD([subQ15,subQ14,subQ13,subQ12,subQ11,subQ10,subQ29,subQ28,subQ27,subQ26,subQ25,subQ24,subQ23,subQ9,subQ8,subQ22,subQ21,subQ20,subQ19,subQ18,subQ17,subQ16,subQ7,subQ6]),ownerDisambiguation([makeQuery(id+"F6.opExtrude","SWEPT_BODY",BODY,{"disambiguationData":[OSD([subQ15,subQ14,subQ13,subQ12,subQ11,subQ10,subQ9,subQ8,subQ7,subQ6,subQ5,subQ4,subQ3,subQ2,subQ1,subQ0]),TDD([makeQuery(id+"F4.opShell","OFFSET_FACE",FACE,{"disambiguationData":[OSD([subQ15,subQ14,subQ13,subQ12,subQ11,subQ10,subQ9,subQ8,subQ7,subQ6,subQ5,subQ4,subQ3,subQ2,subQ1,subQ0]),OD(1.0)]})])]})])],"isStart":false}),makeQuery(id+"F6.opExtrude","CAP_FACE",FACE,{"disambiguationData":[OSD([subQ15,subQ14,subQ13,subQ12,subQ11,subQ10,subQ29,subQ28,subQ27,subQ26,subQ25,subQ24,subQ23,subQ9,subQ8,subQ22,subQ21,subQ20,subQ19,subQ18,subQ17,subQ16,subQ7,subQ6]),ownerDisambiguation([makeQuery(id+"F6.opExtrude","SWEPT_BODY",BODY,{"disambiguationData":[OSD([subQ15,subQ14,subQ13,subQ12,subQ11,subQ10,subQ9,subQ8,subQ7,subQ6,subQ5,subQ4,subQ3,subQ2,subQ1,subQ0]),TDD([makeQuery(id+"F4.opShell","OFFSET_FACE",FACE,{"disambiguationData":[OSD([subQ15,subQ14,subQ13,subQ12,subQ11,subQ10,subQ9,subQ8,subQ7,subQ6,subQ5,subQ4,subQ3,subQ2,subQ1,subQ0]),OD(2.0)]})])]})])],"isStart":false}),makeQuery(id+"F6.opExtrude","CAP_FACE",FACE,{"disambiguationData":[OSD([subQ15,subQ14,subQ13,subQ12,subQ11,subQ10,subQ29,subQ28,subQ27,subQ26,subQ25,subQ24,subQ23,subQ9,subQ8,subQ22,subQ21,subQ20,subQ19,subQ18,subQ17,subQ16,subQ7,subQ6]),ownerDisambiguation([makeQuery(id+"F6.opExtrude","SWEPT_BODY",BODY,{"disambiguationData":[OSD([subQ15,subQ14,subQ13,subQ12,subQ11,subQ10,subQ9,subQ8,subQ7,subQ6,subQ5,subQ4,subQ3,subQ2,subQ1,subQ0]),TDD([makeQuery(id+"F4.opShell","OFFSET_FACE",FACE,{"disambiguationData":[OSD([subQ15,subQ14,subQ13,subQ12,subQ11,subQ10,subQ9,subQ8,subQ7,subQ6,subQ5,subQ4,subQ3,subQ2,subQ1,subQ0]),OD(3.0)]})])]})])],"isStart":false}),makeQuery(id+"F6.opExtrude","CAP_FACE",FACE,{"disambiguationData":[OSD([subQ15,subQ14,subQ13,subQ12,subQ11,subQ10,subQ29,subQ28,subQ27,subQ26,subQ25,subQ24,subQ23,subQ9,subQ8,subQ22,subQ21,subQ20,subQ19,subQ18,subQ17,subQ16,subQ7,subQ6]),ownerDisambiguation([makeQuery(id+"F6.opExtrude","SWEPT_BODY",BODY,{"disambiguationData":[OSD([subQ15,subQ14,subQ13,subQ12,subQ11,subQ10,subQ9,subQ8,subQ7,subQ6,subQ5,subQ4,subQ3,subQ2,subQ1,subQ0]),TDD([makeQuery(id+"F4.opShell","OFFSET_FACE",FACE,{"disambiguationData":[OSD([subQ15,subQ14,subQ13,subQ12,subQ11,subQ10,subQ9,subQ8,subQ7,subQ6,subQ5,subQ4,subQ3,subQ2,subQ1,subQ0]),OD(4.0)]})])]})])],"isStart":false})]});}
            var sketch = newSketch(context, id + "F9", { "sketchPlane" : qUnion([Q0])});
            skLineSegment(sketch, "E34", {"start": v(0, 0) * mm, "end": v(81.1, -73.03) * mm, "construction": true});
            skLineSegment(sketch, "E35.bottom", {"start": v(42.14, 11.11) * mm, "end": v(38.97, 11.11) * mm});
            skLineSegment(sketch, "E35.top", {"start": v(42.14, -84.14) * mm, "end": v(38.97, -84.14) * mm});
            skLineSegment(sketch, "E35.left", {"start": v(42.14, 11.11) * mm, "end": v(42.14, -84.14) * mm});
            skLineSegment(sketch, "E35.right", {"start": v(38.97, 11.11) * mm, "end": v(38.97, -84.14) * mm});
            skPoint(sketch, "E35.middle", {"position": v(40.55, -36.51) * mm});
            skLineSegment(sketch, "E36.bottom", {"start": v(92.22, -38.1) * mm, "end": v(-11.11, -38.1) * mm});
            skLineSegment(sketch, "E36.top", {"start": v(92.22, -34.92) * mm, "end": v(-11.11, -34.92) * mm});
            skLineSegment(sketch, "E36.left", {"start": v(92.22, -38.1) * mm, "end": v(92.22, -34.92) * mm});
            skLineSegment(sketch, "E36.right", {"start": v(-11.11, -38.1) * mm, "end": v(-11.11, -34.92) * mm});
            skSolve(sketch);
        }
        {
            var Q0;
            Q0 = qSketchRegion(id + "F9", true);
            var Q1;
            Q1=makeQuery(id+"F3.opExtrude","CAP_FACE",FACE,{"disambiguationData":[OSD([sQuery(id+"F0.wireOp",EDGE,"E0"),sQuery(id+"F0.wireOp",EDGE,"E2.left"),sQuery(id+"F0.wireOp",EDGE,"E2.right"),sQuery(id+"F0.wireOp",EDGE,"E5"),sQuery(id+"F0.wireOp",EDGE,"E6"),sQuery(id+"F0.wireOp",EDGE,"E7"),sQuery(id+"F0.wireOp",EDGE,"E15"),sQuery(id+"F0.wireOp",EDGE,"E16"),sQuery(id+"F0.wireOp",EDGE,"E27"),sQuery(id+"F0.wireOp",EDGE,"E28"),sQuery(id+"F2.wireOp",EDGE,"E29.bottom"),sQuery(id+"F2.wireOp",EDGE,"E29.top"),sQuery(id+"F2.wireOp",EDGE,"E30"),sQuery(id+"F2.wireOp",EDGE,"E31"),sQuery(id+"F2.wireOp",EDGE,"E32"),sQuery(id+"F2.wireOp",EDGE,"E33")])],"isStart":false});
            extrude(context, id + "F10", {"entities" : qUnion([Q0]), "operationType" : NewBodyOperationType.ADD, "endBound" : BoundingType.UP_TO_SURFACE, "oppositeDirection" : true, "endBoundEntityFace" : qUnion([Q1]), "depth" : 25.4 * mm});
        }
    });
